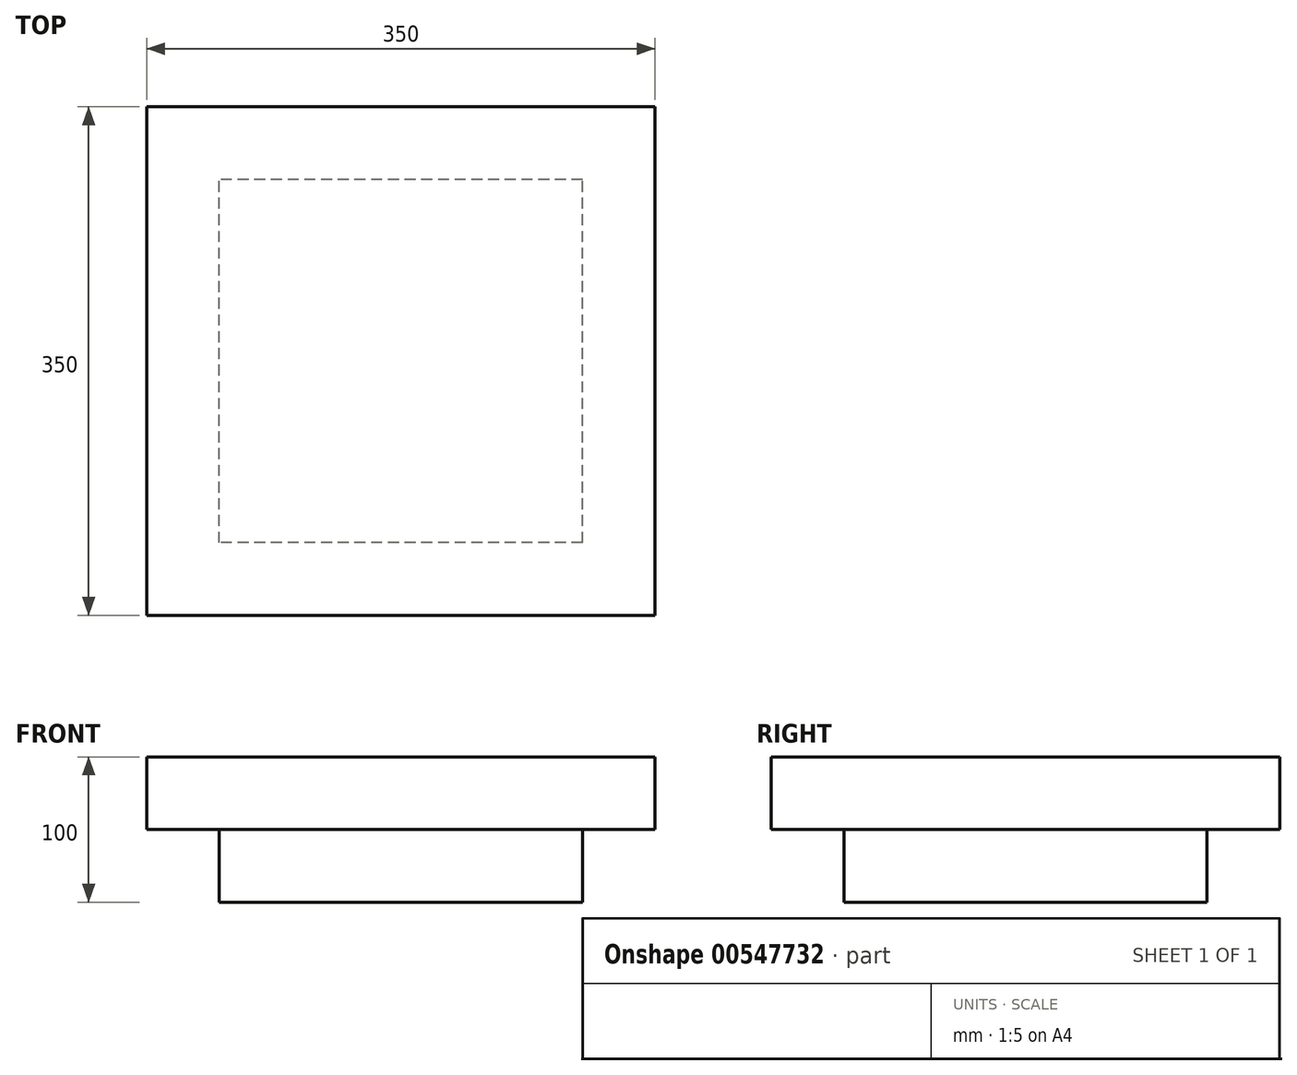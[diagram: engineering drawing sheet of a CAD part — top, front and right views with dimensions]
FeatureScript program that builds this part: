
annotation { "Feature Type Name" : "Feature", "Feature Type Description" : "" }
export const myFeature = defineFeature(function(context is Context, id is Id, definition is map)
    precondition{}
    {
        {
            var Q0;
            Q0=qCreatedBy(makeId("Top.planeOp"),FACE);
            var sketch = newSketch(context, id + "F0", { "sketchPlane" : qUnion([Q0])});
            skLineSegment(sketch, "E0.bottom", {"start": v(175, 175) * mm, "end": v(-175, 175) * mm});
            skLineSegment(sketch, "E0.top", {"start": v(175, -175) * mm, "end": v(-175, -175) * mm});
            skLineSegment(sketch, "E0.left", {"start": v(175, 175) * mm, "end": v(175, -175) * mm});
            skLineSegment(sketch, "E0.right", {"start": v(-175, 175) * mm, "end": v(-175, -175) * mm});
            skPoint(sketch, "E0.middle", {"position": v(0, 0) * mm});
            skSolve(sketch);
        }
        {
            var Q0;
            Q0 = qSketchRegion(id + "F0", true);
            extrude(context, id + "F1", {"entities" : qUnion([Q0]), "depth" : 50 * mm, "offsetDistance" : 25 * mm});
        }
        {
            var Q0;
            Q0=qCreatedBy(makeId("Top.planeOp"),FACE);
            var sketch = newSketch(context, id + "F2", { "sketchPlane" : qUnion([Q0])});
            skLineSegment(sketch, "E1.bottom", {"start": v(125, -125) * mm, "end": v(-125, -125) * mm});
            skLineSegment(sketch, "E1.top", {"start": v(125, 125) * mm, "end": v(-125, 125) * mm});
            skLineSegment(sketch, "E1.left", {"start": v(125, -125) * mm, "end": v(125, 125) * mm});
            skLineSegment(sketch, "E1.right", {"start": v(-125, -125) * mm, "end": v(-125, 125) * mm});
            skPoint(sketch, "E1.middle", {"position": v(0, 0) * mm});
            skSolve(sketch);
        }
        {
            var Q0;
            Q0 = qSketchRegion(id + "F2", true);
            extrude(context, id + "F3", {"entities" : qUnion([Q0]), "operationType" : NewBodyOperationType.ADD, "oppositeDirection" : true, "depth" : 50 * mm, "offsetDistance" : 25 * mm});
        }
    });
